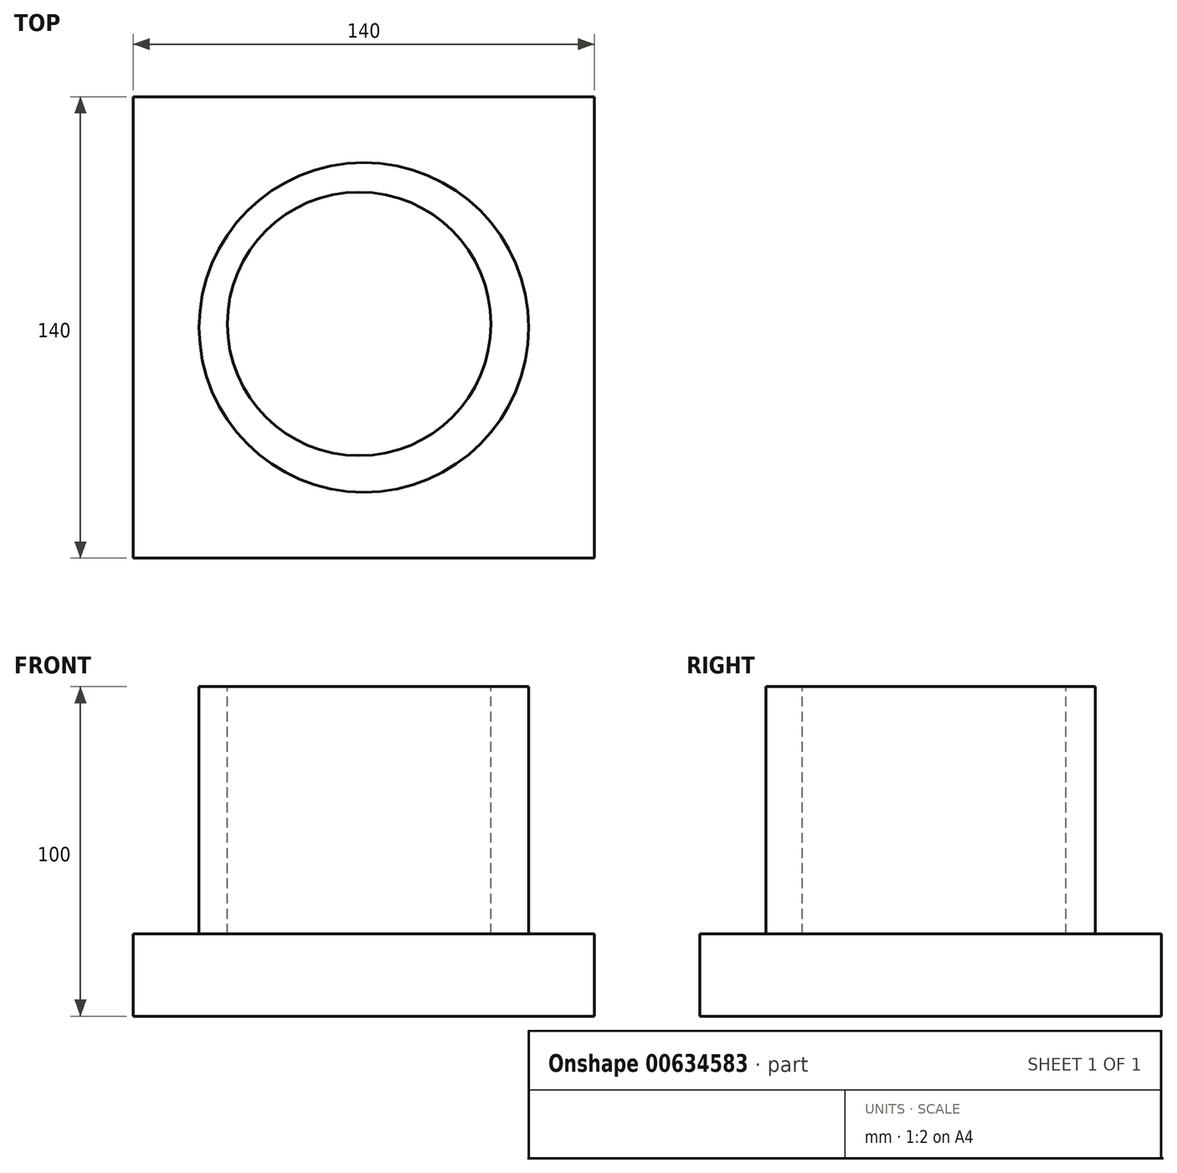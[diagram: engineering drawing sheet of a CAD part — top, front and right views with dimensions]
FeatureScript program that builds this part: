
annotation { "Feature Type Name" : "Feature", "Feature Type Description" : "" }
export const myFeature = defineFeature(function(context is Context, id is Id, definition is map)
    precondition{}
    {
        {
            var Q0;
            Q0=qCreatedBy(makeId("Top.planeOp"),FACE);
            var sketch = newSketch(context, id + "F0", { "sketchPlane" : qUnion([Q0])});
            skLineSegment(sketch, "E0.bottom", {"start": v(-108.31, 94.88) * mm, "end": v(31.69, 94.88) * mm});
            skLineSegment(sketch, "E0.top", {"start": v(-108.31, -45.12) * mm, "end": v(31.69, -45.12) * mm});
            skLineSegment(sketch, "E0.left", {"start": v(-108.31, 94.88) * mm, "end": v(-108.31, -45.12) * mm});
            skLineSegment(sketch, "E0.right", {"start": v(31.69, 94.88) * mm, "end": v(31.69, -45.12) * mm});
            skSolve(sketch);
        }
        {
            var Q0;
            Q0=makeQuery(id+"F0.imprint","IMPRINT",FACE,{"disambiguationData":[TD([[makeQuery(id+"F0.imprint","IMPRINT",EDGE,{"derivedFrom":sQuery(id+"F0.wireOp",EDGE,"E0.bottom")}),-1.0]])]});
            extrude(context, id + "F1", {"entities" : qUnion([Q0]), "depth" : 25 * mm, "offsetDistance" : 25 * mm});
        }
        {
            var Q0;
            Q0=makeQuery(id+"F1.opExtrude","CAP_FACE",FACE,{"disambiguationData":[OSD([sQuery(id+"F0.wireOp",EDGE,"E0.bottom"),sQuery(id+"F0.wireOp",EDGE,"E0.top"),sQuery(id+"F0.wireOp",EDGE,"E0.left"),sQuery(id+"F0.wireOp",EDGE,"E0.right")])],"isStart":false});
            var sketch = newSketch(context, id + "F2", { "sketchPlane" : qUnion([Q0])});
            skLineSegment(sketch, "E1", {"start": v(31.69, 24.88) * mm, "end": v(-108.31, 24.88) * mm, "construction": true});
            skCircle(sketch, "E2", {"center": v(-38.31, 24.88) * mm, "radius": 50 * mm});
            skSolve(sketch);
        }
        {
            var Q0;
            Q0=makeQuery(id+"F2.imprint","IMPRINT",FACE,{"disambiguationData":[TD([[makeQuery(id+"F2.imprint","IMPRINT",EDGE,{"derivedFrom":sQuery(id+"F2.wireOp",EDGE,"E2")}),1.0]])]});
            extrude(context, id + "F3", {"entities" : qUnion([Q0]), "operationType" : NewBodyOperationType.ADD, "depth" : 75 * mm, "offsetDistance" : 25 * mm});
        }
        {
            var Q0;
            Q0=makeQuery(id+"F3.opExtrude","CAP_FACE",FACE,{"disambiguationData":[OSD([sQuery(id+"F2.wireOp",EDGE,"E2")])],"isStart":false});
            var sketch = newSketch(context, id + "F4", { "sketchPlane" : qUnion([Q0])});
            skLineSegment(sketch, "E3.bottom", {"start": v(-69.58, -14.13) * mm, "end": v(-9.9, -14.13) * mm, "construction": true});
            skLineSegment(sketch, "E3.top", {"start": v(-69.58, 66.03) * mm, "end": v(-9.9, 66.03) * mm, "construction": true});
            skLineSegment(sketch, "E3.left", {"start": v(-69.58, -14.13) * mm, "end": v(-69.58, 66.03) * mm, "construction": true});
            skLineSegment(sketch, "E3.right", {"start": v(-9.9, -14.13) * mm, "end": v(-9.9, 66.03) * mm, "construction": true});
            skLineSegment(sketch, "E4", {"start": v(-69.58, 25.95) * mm, "end": v(-9.9, 25.95) * mm, "construction": true});
            skCircle(sketch, "E5", {"center": v(-39.74, 25.95) * mm, "radius": 40 * mm});
            skSolve(sketch);
        }
        {
            var Q0;
            Q0=makeQuery(id+"F4.imprint","IMPRINT",FACE,{"disambiguationData":[TD([[makeQuery(id+"F4.imprint","IMPRINT",EDGE,{"derivedFrom":sQuery(id+"F4.wireOp",EDGE,"E5")}),1.0]])]});
            extrude(context, id + "F5", {"entities" : qUnion([Q0]), "operationType" : NewBodyOperationType.REMOVE, "oppositeDirection" : true, "depth" : 75 * mm, "offsetDistance" : 25 * mm});
        }
    });
